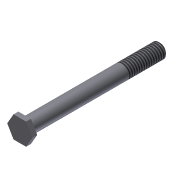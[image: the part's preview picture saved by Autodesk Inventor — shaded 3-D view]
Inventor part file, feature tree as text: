
AUTODESK INVENTOR PART (.ipt)
format: ipt  version: 2011 (Build 150239000, 239)  size: 87,552 bytes
history: native  units: in
note: dims shown in document units (in); Inventor stores cm internally (conversion verified against a paired STEP export)
features: extrude x2, sketch x2, thread x1, chamfer x1
ambient origin geometry x8: Origin, YZ Plane, XZ Plane, XY Plane, X Axis, Y Axis, Z Axis, Center Point
bodies: Solid1 (feature_tree)
feature tree (6):
  extrude  "Extrusion1"  Depth=3.5in TaperAngle=0.0deg
  extrude  "Extrusion2"  Depth=0.125in TaperAngle=0.0deg
  thread  "Thread1"  [1 undecoded]
  chamfer  "Chamfer1"  Distance=0.04in Angle=45.0deg
  sketch  "Sketch1"  dims[d0=0.375in d1=3.5in d2=0.0in]
  sketch  "Sketch2"  dims[d3=0.5625in d4=0.125in d5=0.0in d6=1.0in d7=0.0in d8=0.04in d9=0.125in d10=45.0deg]
note: 1 required parameter value undecoded (feature->parameter linkage not recoverable at this tier; creation-order binding heuristic only, values carry confidence <= 0.55)
